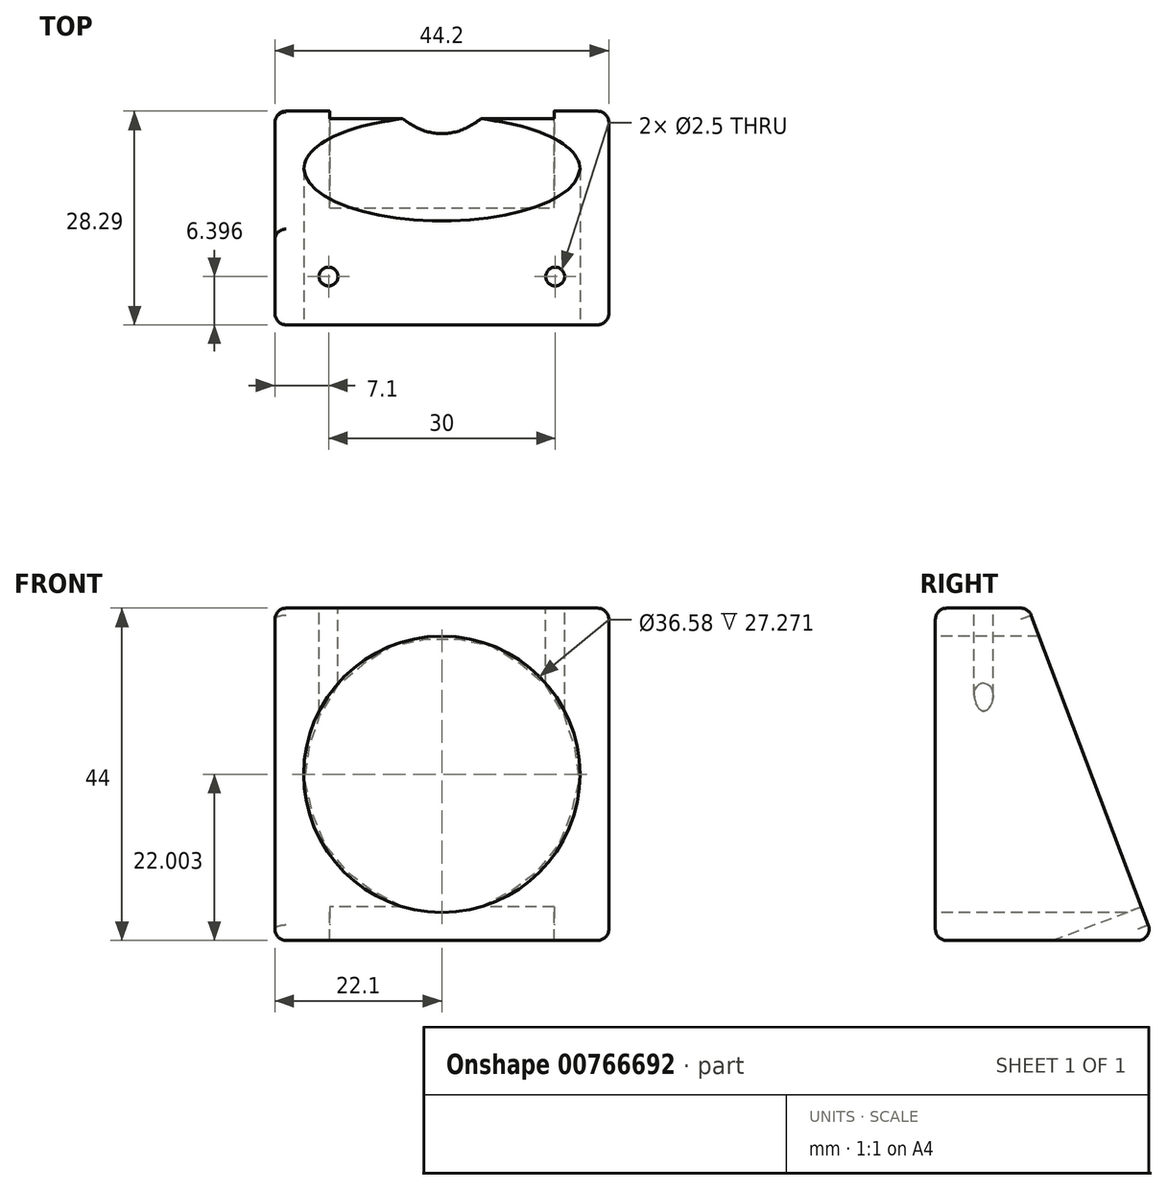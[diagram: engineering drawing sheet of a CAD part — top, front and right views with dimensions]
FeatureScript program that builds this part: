
annotation { "Feature Type Name" : "Feature", "Feature Type Description" : "" }
export const myFeature = defineFeature(function(context is Context, id is Id, definition is map)
    precondition{}
    {
        {
            var Q0;
            Q0=qCreatedBy(makeId("Front.planeOp"),FACE);
            var sketch = newSketch(context, id + "F0", { "sketchPlane" : qUnion([Q0])});
            skLineSegment(sketch, "E0.bottom", {"start": v(14.85, 2.06) * mm, "end": v(-14.85, 2.06) * mm});
            skLineSegment(sketch, "E0.top", {"start": v(14.85, -2.06) * mm, "end": v(-14.85, -2.06) * mm});
            skLineSegment(sketch, "E0.left", {"start": v(14.85, 2.06) * mm, "end": v(14.85, -2.06) * mm});
            skLineSegment(sketch, "E0.right", {"start": v(-14.85, 2.06) * mm, "end": v(-14.85, -2.06) * mm});
            skPoint(sketch, "E0.middle", {"position": v(0, 0) * mm});
            skSolve(sketch);
        }
        {
            var Q0;
            Q0=qCreatedBy(makeId("Right.planeOp"),FACE);
            var sketch = newSketch(context, id + "F1", { "sketchPlane" : qUnion([Q0])});
            skLineSegment(sketch, "E1", {"start": v(-26.37, 41.94) * mm, "end": v(-26.37, -2.06) * mm});
            skLineSegment(sketch, "E2", {"start": v(-26.37, -2.06) * mm, "end": v(2.6, -2.06) * mm});
            skLineSegment(sketch, "E3", {"start": v(2.6, -2.06) * mm, "end": v(-14.05, 41.94) * mm});
            skLineSegment(sketch, "E4", {"start": v(-14.05, 41.94) * mm, "end": v(-26.37, 41.94) * mm});
            skLineSegment(sketch, "E5.0", {"start": v(-14.74, 40.94) * mm, "end": v(-25.37, 40.94) * mm});
            skLineSegment(sketch, "E5.1", {"start": v(1.14, -1.06) * mm, "end": v(-14.74, 40.94) * mm});
            skLineSegment(sketch, "E5.2", {"start": v(-25.37, -1.06) * mm, "end": v(1.14, -1.06) * mm});
            skLineSegment(sketch, "E5.3", {"start": v(-25.37, 40.94) * mm, "end": v(-25.37, -1.06) * mm});
            skSolve(sketch);
        }
        {
            var Q0;
            Q0=qCreatedBy(makeId("Right.planeOp"),FACE);
            var sketch = newSketch(context, id + "F2", { "sketchPlane" : qUnion([Q0])});
            skLineSegment(sketch, "E6.0", {"start": v(-14.05, 41.94) * mm, "end": v(-26.37, 41.94) * mm});
            skLineSegment(sketch, "E7.0", {"start": v(-26.37, 41.94) * mm, "end": v(-26.37, -2.06) * mm});
            skLineSegment(sketch, "E8.0", {"start": v(-26.37, -2.06) * mm, "end": v(2.6, -2.06) * mm});
            skLineSegment(sketch, "E9.0", {"start": v(2.6, -2.06) * mm, "end": v(-14.05, 41.94) * mm});
            skSolve(sketch);
        }
        {
            var Q0;
            Q0=qSketchRegion(id+"F2",true);
            extrude(context, id + "F3", {"entities" : qUnion([Q0]), "endBound" : BoundingType.SYMMETRIC, "depth" : 44.2 * mm, "offsetDistance" : 25.4 * mm});
        }
        {
            var Q0;
            Q0=makeQuery(id+"F3.opExtrude","SWEPT_EDGE",EDGE,{"disambiguationData":[OSD([sQuery(id+"F2.wireOp",EDGE,"E8.0"),sQuery(id+"F2.wireOp",EDGE,"E9.0")])]});
            var Q1;
            Q1=makeQuery(id+"F3.opExtrude","CAP_EDGE",EDGE,{"disambiguationData":[OSD([sQuery(id+"F2.wireOp",EDGE,"E7.0")])],"isStart":false});
            var Q2;
            Q2=makeQuery(id+"F3.opExtrude","CAP_EDGE",EDGE,{"disambiguationData":[OSD([sQuery(id+"F2.wireOp",EDGE,"E9.0")])],"isStart":true});
            var Q3;
            Q3=makeQuery(id+"F3.opExtrude","CAP_EDGE",EDGE,{"disambiguationData":[OSD([sQuery(id+"F2.wireOp",EDGE,"E7.0")])],"isStart":true});
            fillet(context, id + "F4", {"entities" : qUnion([Q0, Q1, Q2, Q3]), "radius" : 1.5 * mm, "tangentPropagation" : true, "allowEdgeOverflow" : false});
        }
        {
            var Q0;
            Q0=makeQuery(id+"F3.opExtrude","CAP_EDGE",EDGE,{"disambiguationData":[OSD([sQuery(id+"F2.wireOp",EDGE,"E9.0")])],"isStart":false});
            var Q1;
            {var subQ0=sQuery(id+"F2.wireOp",EDGE,"E9.0");Q1=makeQuery(id+"F4.opFillet","BLEND_EDGE",EDGE,{"blendedFrom":[makeQuery(id+"F3.opExtrude","CAP_EDGE",EDGE,{"disambiguationData":[OSD([subQ0])],"isStart":true}),makeQuery(id+"F3.opExtrude","SWEPT_FACE",FACE,{"disambiguationData":[OSD([subQ0])]})],"blendedInto":[makeQuery(id+"F3.opExtrude","SWEPT_FACE",FACE,{"disambiguationData":[OSD([subQ0])]})]});}
            var Q2;
            Q2=makeQuery(id+"F3.opExtrude","CAP_EDGE",EDGE,{"disambiguationData":[OSD([sQuery(id+"F2.wireOp",EDGE,"E6.0")])],"isStart":false});
            fillet(context, id + "F5", {"entities" : qUnion([Q0, Q1, Q2]), "radius" : 1.5 * mm, "tangentPropagation" : true, "allowEdgeOverflow" : false});
        }
        {
            var Q0;
            Q0=makeQuery(id+"F3.opExtrude","SWEPT_FACE",FACE,{"disambiguationData":[OSD([sQuery(id+"F2.wireOp",EDGE,"E7.0")])]});
            var sketch = newSketch(context, id + "F6", { "sketchPlane" : qUnion([Q0])});
            skCircle(sketch, "E10", {"center": v(0, 19.94) * mm, "radius": 18.29 * mm});
            skPoint(sketch, "E11.0", {"position": v(0, 41.94) * mm});
            skPoint(sketch, "E12.0", {"position": v(0, -2.06) * mm});
            skLineSegment(sketch, "E13", {"start": v(0, 41.94) * mm, "end": v(0, -2.06) * mm, "construction": true});
            skSolve(sketch);
        }
        {
            var Q0;
            Q0=qSketchRegion(id+"F6",true);
            extrude(context, id + "F7", {"entities" : qUnion([Q0]), "operationType" : NewBodyOperationType.REMOVE, "endBound" : BoundingType.UP_TO_NEXT, "oppositeDirection" : true, "depth" : 25.4 * mm, "offsetDistance" : 25.4 * mm});
        }
        {
            var Q0;
            Q0=qCreatedBy(makeId("Front.planeOp"),FACE);
            var sketch = newSketch(context, id + "F8", { "sketchPlane" : qUnion([Q0])});
            skPoint(sketch, "E14.0", {"position": v(14.85, -2.06) * mm});
            skPoint(sketch, "E15.0", {"position": v(-14.85, -2.06) * mm});
            skLineSegment(sketch, "E16.bottom", {"start": v(14.85, -2.06) * mm, "end": v(-14.85, -2.06) * mm});
            skLineSegment(sketch, "E16.top", {"start": v(14.85, -0.03) * mm, "end": v(-14.85, -0.03) * mm});
            skLineSegment(sketch, "E16.left", {"start": v(14.85, -2.06) * mm, "end": v(14.85, -0.03) * mm});
            skLineSegment(sketch, "E16.right", {"start": v(-14.85, -2.06) * mm, "end": v(-14.85, -0.03) * mm});
            skSolve(sketch);
        }
        {
            var Q0;
            Q0=qSketchRegion(id+"F8",true);
            extrude(context, id + "F9", {"entities" : qUnion([Q0]), "operationType" : NewBodyOperationType.REMOVE, "endBound" : BoundingType.THROUGH_ALL, "oppositeDirection" : true, "depth" : 25.4 * mm, "offsetDistance" : 25.4 * mm});
        }
        {
            var Q0;
            Q0=makeQuery(id+"F3.opExtrude","SWEPT_FACE",FACE,{"disambiguationData":[OSD([sQuery(id+"F2.wireOp",EDGE,"E9.0")])]});
            var sketch = newSketch(context, id + "F10", { "sketchPlane" : qUnion([Q0])});
            skPoint(sketch, "E17.0", {"position": v(14.85, 1.92) * mm});
            skPoint(sketch, "E18.0", {"position": v(-14.85, 1.92) * mm});
            skLineSegment(sketch, "E19.bottom", {"start": v(-14.85, 1.92) * mm, "end": v(14.85, 1.92) * mm});
            skLineSegment(sketch, "E19.top", {"start": v(-14.85, -2.84) * mm, "end": v(14.85, -2.84) * mm});
            skLineSegment(sketch, "E19.left", {"start": v(-14.85, 1.92) * mm, "end": v(-14.85, -2.84) * mm});
            skLineSegment(sketch, "E19.right", {"start": v(14.85, 1.92) * mm, "end": v(14.85, -2.84) * mm});
            skSolve(sketch);
        }
        {
            var Q0;
            Q0=qSketchRegion(id+"F10",true);
            extrude(context, id + "F11", {"entities" : qUnion([Q0]), "operationType" : NewBodyOperationType.REMOVE, "endBound" : BoundingType.UP_TO_NEXT, "oppositeDirection" : true, "depth" : 25.4 * mm, "offsetDistance" : 25.4 * mm});
        }
        {
            var Q0;
            Q0=makeQuery(id+"F3.opExtrude","SWEPT_FACE",FACE,{"disambiguationData":[OSD([sQuery(id+"F2.wireOp",EDGE,"E6.0")])]});
            var sketch = newSketch(context, id + "F12", { "sketchPlane" : qUnion([Q0])});
            skLineSegment(sketch, "E20", {"start": v(-15, -19.97) * mm, "end": v(15, -19.97) * mm, "construction": true});
            skCircle(sketch, "E21", {"center": v(-15, -19.97) * mm, "radius": 1.25 * mm});
            skCircle(sketch, "E22", {"center": v(15, -19.97) * mm, "radius": 1.25 * mm});
            skLineSegment(sketch, "E23", {"start": v(0, 0) * mm, "end": v(0, -19.97) * mm, "construction": true});
            skLineSegment(sketch, "E24", {"start": v(15, -19.97) * mm, "end": v(20.6, -19.97) * mm, "construction": true});
            skSolve(sketch);
        }
        {
            var Q0;
            Q0=qSketchRegion(id+"F12",true);
            extrude(context, id + "F13", {"entities" : qUnion([Q0]), "operationType" : NewBodyOperationType.REMOVE, "endBound" : BoundingType.UP_TO_NEXT, "oppositeDirection" : true, "depth" : 25.4 * mm, "offsetDistance" : 25.4 * mm});
        }
    });
